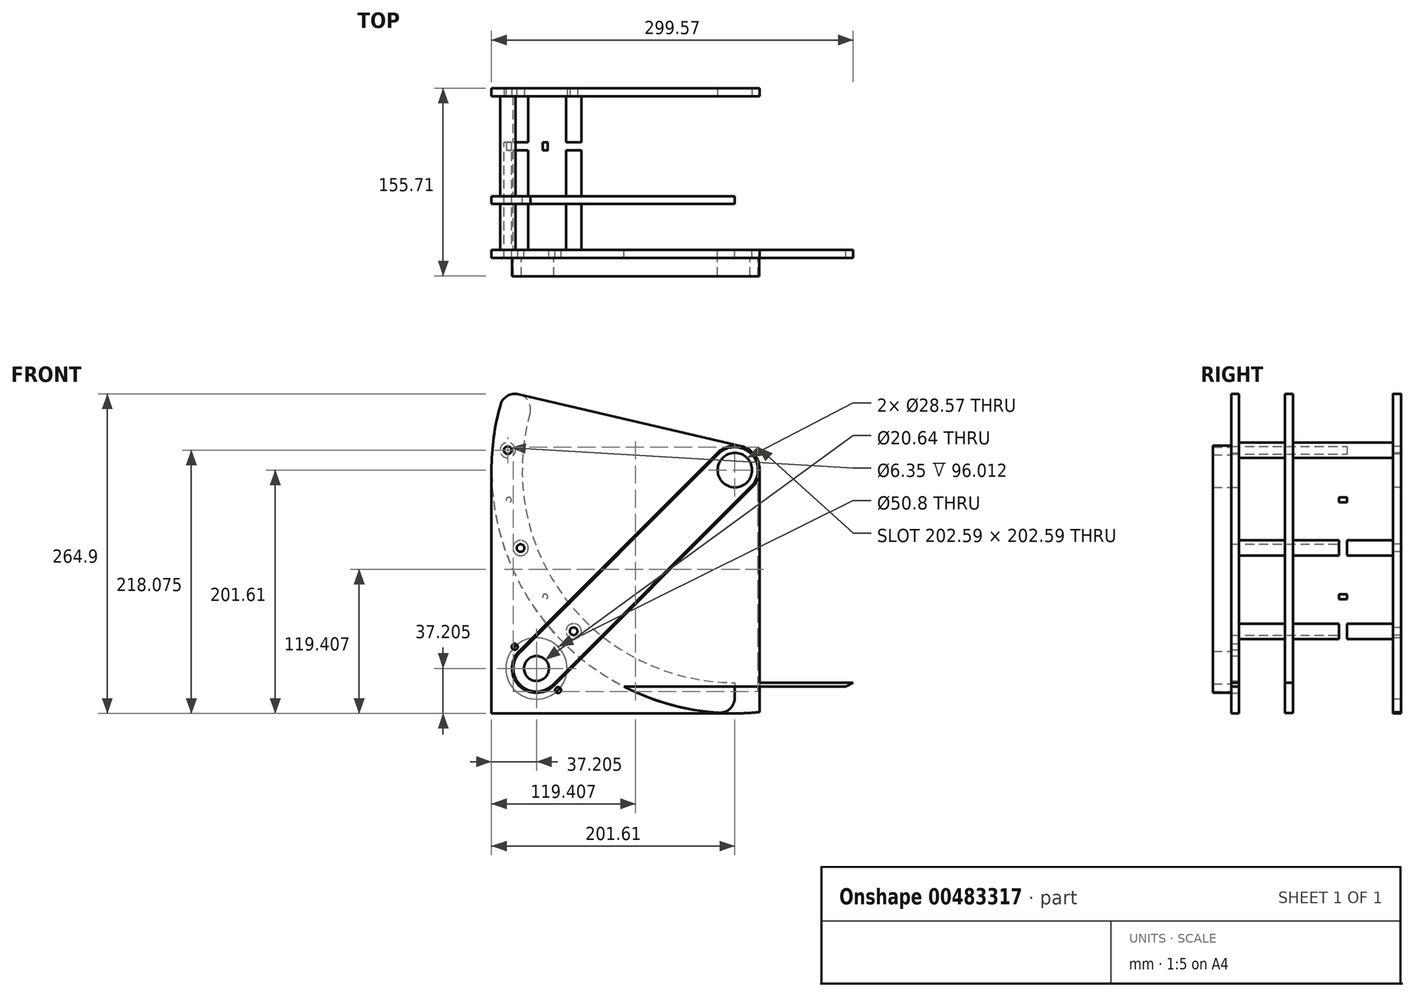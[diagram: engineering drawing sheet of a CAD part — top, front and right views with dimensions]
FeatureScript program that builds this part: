
annotation { "Feature Type Name" : "Feature", "Feature Type Description" : "" }
export const myFeature = defineFeature(function(context is Context, id is Id, definition is map)
    precondition{}
    {
        {
            var Q0;
            Q0=qCreatedBy(makeId("Front.planeOp"),FACE);
            var sketch = newSketch(context, id + "F0", { "sketchPlane" : qUnion([Q0])});
            skCircle(sketch, "E0", {"center": v(0, 0) * mm, "radius": 61.91 * mm});
            skCircle(sketch, "E1", {"center": v(0, 0) * mm, "radius": 176.21 * mm});
            skCircle(sketch, "E2.cCircle", {"center": v(0, 0) * mm, "radius": 6.35 * mm, "construction": true});
            skLineSegment(sketch, "E2.0", {"start": v(-3.67, 6.35) * mm, "end": v(3.67, 6.35) * mm});
            skLineSegment(sketch, "E2.1", {"start": v(3.67, 6.35) * mm, "end": v(7.33, 0) * mm});
            skLineSegment(sketch, "E2.2", {"start": v(7.33, 0) * mm, "end": v(3.67, -6.35) * mm});
            skLineSegment(sketch, "E2.3", {"start": v(3.67, -6.35) * mm, "end": v(-3.67, -6.35) * mm});
            skLineSegment(sketch, "E2.4", {"start": v(-3.67, -6.35) * mm, "end": v(-7.33, 0) * mm});
            skLineSegment(sketch, "E2.5", {"start": v(-7.33, 0) * mm, "end": v(-3.67, 6.35) * mm});
            skPoint(sketch, "E2.0.midPoint", {"position": v(0, 6.35) * mm});
            skCircle(sketch, "E3", {"center": v(0, 0) * mm, "radius": 201.61 * mm});
            skLineSegment(sketch, "E4", {"start": v(0, -176.21) * mm, "end": v(267.79, -176.21) * mm});
            skCircle(sketch, "E5", {"center": v(0, 0) * mm, "radius": 188.91 * mm, "construction": true});
            skCircle(sketch, "E6", {"center": v(-133.58, -133.58) * mm, "radius": 3.18 * mm});
            skLineSegment(sketch, "E7", {"start": v(0, 0) * mm, "end": v(-133.58, -133.58) * mm, "construction": true});
            skLineSegment(sketch, "E8", {"start": v(0, 0) * mm, "end": v(-190.63, 65.64) * mm});
            skCircle(sketch, "E9.1.0", {"center": v(-177.52, -64.61) * mm, "radius": 3.18 * mm});
            skCircle(sketch, "E9.2.0", {"center": v(-188.2, 16.46) * mm, "radius": 3.18 * mm});
            skCircle(sketch, "E9.3.0", {"center": v(-163.6, 94.46) * mm, "radius": 3.18 * mm});
            skLineSegment(sketch, "E9.anchor2", {"start": v(0, 0) * mm, "end": v(-163.6, 94.46) * mm, "construction": true});
            skLineSegment(sketch, "E10", {"start": v(267.83, -179.39) * mm, "end": v(-92.02, -179.39) * mm});
            skLineSegment(sketch, "E11", {"start": v(267.79, -176.21) * mm, "end": v(267.83, -179.39) * mm});
            skCircle(sketch, "E12", {"center": v(0, 0) * mm, "radius": 14.29 * mm});
            skCircle(sketch, "E13", {"center": v(0, 0) * mm, "radius": 20.64 * mm});
            skLineSegment(sketch, "E14", {"start": v(4.69, 20.1) * mm, "end": v(-190.63, 65.64) * mm});
            skLineSegment(sketch, "E15", {"start": v(20.64, 0) * mm, "end": v(20.64, -176.21) * mm});
            skLineSegment(sketch, "E16", {"start": v(20.64, -175.98) * mm, "end": v(20.64, -200.55) * mm});
            skLineSegment(sketch, "E17", {"start": v(-201.61, 0) * mm, "end": v(-201.61, -201.61) * mm});
            skLineSegment(sketch, "E18", {"start": v(-201.61, -201.61) * mm, "end": v(0, -201.61) * mm});
            skCircle(sketch, "E19", {"center": v(-164.4, -164.4) * mm, "radius": 10.32 * mm});
            skCircle(sketch, "E20", {"center": v(-146.44, -182.37) * mm, "radius": 2.49 * mm});
            skCircle(sketch, "E21", {"center": v(-182.37, -146.44) * mm, "radius": 2.49 * mm});
            skCircle(sketch, "E22", {"center": v(-164.4, -164.4) * mm, "radius": 25.4 * mm, "construction": true});
            skLineSegment(sketch, "E23", {"start": v(-146.44, -182.37) * mm, "end": v(-182.37, -146.44) * mm, "construction": true});
            skCircle(sketch, "E24", {"center": v(-164.4, -164.4) * mm, "radius": 19.1 * mm});
            skCircle(sketch, "E25", {"center": v(0, 0) * mm, "radius": 19.1 * mm});
            skLineSegment(sketch, "E26", {"start": v(-201.61, -201.61) * mm, "end": v(-133.58, -133.58) * mm, "construction": true});
            skSolve(sketch);
        }
        {
            var Q0;
            {var subQ0=sQuery(id+"F0.wireOp",EDGE,"E8");var subQ1=sQuery(id+"F0.wireOp",EDGE,"E0");var subQ2=makeQuery(id+"F0.imprint","INTERSECT",VERTEX,{"derivedFrom":[subQ1,subQ0]});Q0=makeQuery(id+"F0.imprint","IMPRINT",FACE,{"disambiguationData":[TD([[makeQuery(id+"F0.imprint","IMPRINT",EDGE,{"disambiguationData":[TD([[subQ2,1.0]])],"derivedFrom":subQ1}),1.0]])]});}
            var Q1;
            {var subQ0=sQuery(id+"F0.wireOp",EDGE,"E8");var subQ1=sQuery(id+"F0.wireOp",EDGE,"E0");var subQ2=makeQuery(id+"F0.imprint","INTERSECT",VERTEX,{"derivedFrom":[subQ1,subQ0]});Q1=makeQuery(id+"F0.imprint","IMPRINT",FACE,{"disambiguationData":[TD([[makeQuery(id+"F0.imprint","IMPRINT",EDGE,{"disambiguationData":[TD([[subQ2,1.0]])],"derivedFrom":subQ1}),-1.0]])]});}
            var Q2;
            {var subQ0=sQuery(id+"F0.wireOp",EDGE,"E8");var subQ1=sQuery(id+"F0.wireOp",EDGE,"E0");var subQ2=makeQuery(id+"F0.imprint","INTERSECT",VERTEX,{"derivedFrom":[subQ1,subQ0]});Q2=makeQuery(id+"F0.imprint","IMPRINT",FACE,{"disambiguationData":[TD([[makeQuery(id+"F0.imprint","IMPRINT",EDGE,{"disambiguationData":[TD([[subQ2,-1.0]])],"derivedFrom":subQ1}),-1.0]])]});}
            var Q3;
            {var subQ0=sQuery(id+"F0.wireOp",EDGE,"E8");var subQ1=sQuery(id+"F0.wireOp",EDGE,"E1");var subQ2=makeQuery(id+"F0.imprint","INTERSECT",VERTEX,{"derivedFrom":[subQ1,subQ0]});Q3=makeQuery(id+"F0.imprint","IMPRINT",FACE,{"disambiguationData":[TD([[makeQuery(id+"F0.imprint","IMPRINT",EDGE,{"disambiguationData":[TD([[subQ2,1.0]])],"derivedFrom":subQ1}),-1.0]])]});}
            var Q4;
            Q4=makeQuery(id+"F0.imprint","IMPRINT",FACE,{"disambiguationData":[TD([[makeQuery(id+"F0.imprint","IMPRINT",EDGE,{"derivedFrom":sQuery(id+"F0.wireOp",EDGE,"E12")}),-1.0]])]});
            var Q5;
            {var subQ0=sQuery(id+"F0.wireOp",EDGE,"E8");var subQ1=sQuery(id+"F0.wireOp",EDGE,"E0");var subQ2=makeQuery(id+"F0.imprint","INTERSECT",VERTEX,{"derivedFrom":[subQ1,subQ0]});Q5=makeQuery(id+"F0.imprint","IMPRINT",FACE,{"disambiguationData":[TD([[makeQuery(id+"F0.imprint","IMPRINT",EDGE,{"disambiguationData":[TD([[subQ2,-1.0]])],"derivedFrom":subQ1}),1.0]])]});}
            var Q6;
            {var subQ0=sQuery(id+"F0.wireOp",EDGE,"E4");var subQ1=sQuery(id+"F0.wireOp",EDGE,"E1");var subQ2=makeQuery(id+"F0.imprint","INTERSECT",VERTEX,{"derivedFrom":[subQ1,subQ0]});Q6=makeQuery(id+"F0.imprint","IMPRINT",FACE,{"disambiguationData":[TD([[makeQuery(id+"F0.imprint","IMPRINT",EDGE,{"disambiguationData":[TD([[subQ2,-1.0]])],"derivedFrom":subQ1}),-1.0]])]});}
            var Q7;
            {var subQ0=sQuery(id+"F0.wireOp",EDGE,"E10");var subQ1=sQuery(id+"F0.wireOp",EDGE,"E3");var subQ2=makeQuery(id+"F0.imprint","INTERSECT",VERTEX,{"disambiguationData":[OD(0.0)],"derivedFrom":[subQ1,subQ0]});Q7=makeQuery(id+"F0.imprint","IMPRINT",FACE,{"disambiguationData":[TD([[makeQuery(id+"F0.imprint","IMPRINT",EDGE,{"disambiguationData":[TD([[subQ2,-1.0]])],"derivedFrom":subQ1}),1.0]])]});}
            var Q8;
            Q8=makeQuery(id+"F0.imprint","IMPRINT",FACE,{"disambiguationData":[TD([[makeQuery(id+"F0.imprint","IMPRINT",EDGE,{"derivedFrom":sQuery(id+"F0.wireOp",EDGE,"E6")}),-1.0]])]});
            var Q9;
            Q9=makeQuery(id+"F0.imprint","IMPRINT",FACE,{"disambiguationData":[TD([[makeQuery(id+"F0.imprint","IMPRINT",EDGE,{"derivedFrom":sQuery(id+"F0.wireOp",EDGE,"E25")}),-1.0]])]});
            var Q10;
            {var subQ3=sQuery(id+"F0.wireOp",EDGE,"E17");Q10=makeQuery(id+"F0.imprint","IMPRINT",FACE,{"disambiguationData":[TD([[makeQuery(id+"F0.imprint","IMPRINT",EDGE,{"derivedFrom":subQ3}),1.0]])]});}
            var Q11;
            Q11=makeQuery(id+"F0.imprint","IMPRINT",FACE,{"disambiguationData":[TD([[makeQuery(id+"F0.imprint","IMPRINT",EDGE,{"derivedFrom":sQuery(id+"F0.wireOp",EDGE,"E19")}),-1.0]])]});
            extrude(context, id + "F1", {"entities" : qUnion([Q0, Q1, Q2, Q3, Q4, Q5, Q6, Q7, Q8, Q9, Q10, Q11]), "depth" : 6.6 * mm, "offsetDistance" : 25.4 * mm});
        }
        {
            var Q0;
            Q0=makeQuery(id+"F1.opExtrude","CAP_FACE",FACE,{"disambiguationData":[OSD([sQuery(id+"F0.wireOp",EDGE,"E1"),sQuery(id+"F0.wireOp",EDGE,"E3"),sQuery(id+"F0.wireOp",EDGE,"E4"),sQuery(id+"F0.wireOp",EDGE,"E6"),sQuery(id+"F0.wireOp",EDGE,"E8"),sQuery(id+"F0.wireOp",EDGE,"E9.1.0"),sQuery(id+"F0.wireOp",EDGE,"E9.2.0"),sQuery(id+"F0.wireOp",EDGE,"E9.3.0"),sQuery(id+"F0.wireOp",EDGE,"E10")])],"isStart":true});
            var sketch = newSketch(context, id + "F2", { "sketchPlane" : qUnion([Q0])});
            skCircle(sketch, "E27", {"center": v(188.2, 16.46) * mm, "radius": 6.35 * mm});
            skCircle(sketch, "E28", {"center": v(177.52, -64.61) * mm, "radius": 6.35 * mm});
            skCircle(sketch, "E29", {"center": v(133.58, -133.58) * mm, "radius": 6.35 * mm});
            skSolve(sketch);
        }
        {
            var Q0;
            Q0=makeQuery(id+"F2.imprint","IMPRINT",FACE,{"disambiguationData":[TD([[makeQuery(id+"F2.imprint","IMPRINT",EDGE,{"derivedFrom":sQuery(id+"F2.wireOp",EDGE,"E27")}),1.0]])]});
            var Q1;
            Q1=makeQuery(id+"F2.imprint","IMPRINT",FACE,{"disambiguationData":[TD([[makeQuery(id+"F2.imprint","IMPRINT",EDGE,{"derivedFrom":sQuery(id+"F2.wireOp",EDGE,"E28")}),1.0]])]});
            var Q2;
            Q2=makeQuery(id+"F2.imprint","IMPRINT",FACE,{"disambiguationData":[TD([[makeQuery(id+"F2.imprint","IMPRINT",EDGE,{"derivedFrom":sQuery(id+"F2.wireOp",EDGE,"E29")}),1.0]])]});
            extrude(context, id + "F3", {"entities" : qUnion([Q0, Q1, Q2]), "operationType" : NewBodyOperationType.ADD, "depth" : 38.1 * mm, "offsetDistance" : 25.4 * mm});
        }
        {
            var Q0;
            Q0=makeQuery(id+"F3.opExtrude","CAP_FACE",FACE,{"disambiguationData":[OSD([sQuery(id+"F0.wireOp",EDGE,"E6"),sQuery(id+"F2.wireOp",EDGE,"E29")])],"isStart":false});
            var sketch = newSketch(context, id + "F4", { "sketchPlane" : qUnion([Q0])});
            skCircle(sketch, "E30", {"center": v(0, 0) * mm, "radius": 201.61 * mm});
            skCircle(sketch, "E31", {"center": v(0, 0) * mm, "radius": 176.21 * mm});
            skLineSegment(sketch, "E32", {"start": v(133.58, 133.58) * mm, "end": v(0, 0) * mm, "construction": true});
            skCircle(sketch, "E33", {"center": v(0, 0) * mm, "radius": 188.91 * mm, "construction": true});
            skCircle(sketch, "E34.1.0", {"center": v(178.89, 60.72) * mm, "radius": 6.35 * mm});
            skCircle(sketch, "E34.2.0", {"center": v(187.3, -24.66) * mm, "radius": 6.35 * mm});
            skCircle(sketch, "E34.3.0", {"center": v(157.08, -104.95) * mm, "radius": 6.35 * mm});
            skCircle(sketch, "E34.4.0", {"center": v(94.46, -163.6) * mm, "radius": 6.35 * mm});
            skLineSegment(sketch, "E34.anchor1", {"start": v(0, 0) * mm, "end": v(133.58, 133.58) * mm, "construction": true});
            skLineSegment(sketch, "E34.anchor2", {"start": v(0, 0) * mm, "end": v(94.46, -163.6) * mm, "construction": true});
            skLineSegment(sketch, "E35.0", {"start": v(-4.69, 20.1) * mm, "end": v(190.63, 65.64) * mm});
            skCircle(sketch, "E36", {"center": v(178.89, 60.72) * mm, "radius": 3.18 * mm});
            skCircle(sketch, "E37", {"center": v(188.2, 16.46) * mm, "radius": 3.18 * mm});
            skCircle(sketch, "E38", {"center": v(187.3, -24.66) * mm, "radius": 3.18 * mm});
            skCircle(sketch, "E39", {"center": v(177.52, -64.61) * mm, "radius": 3.18 * mm});
            skCircle(sketch, "E40", {"center": v(157.08, -104.95) * mm, "radius": 3.18 * mm});
            skCircle(sketch, "E41", {"center": v(133.58, -133.58) * mm, "radius": 3.18 * mm});
            skLineSegment(sketch, "E42", {"start": v(0, 0) * mm, "end": v(0, -201.61) * mm});
            skSolve(sketch);
        }
        {
            var Q0;
            Q0=makeQuery(id+"F4.imprint","IMPRINT",FACE,{"disambiguationData":[TD([[makeQuery(id+"F4.imprint","IMPRINT",EDGE,{"derivedFrom":sQuery(id+"F4.wireOp",EDGE,"E34.2.0")}),-1.0]])]});
            var Q1;
            Q1=makeQuery(id+"F4.imprint","IMPRINT",FACE,{"disambiguationData":[TD([[makeQuery(id+"F4.imprint","IMPRINT",EDGE,{"derivedFrom":sQuery(id+"F4.wireOp",EDGE,"E41")}),1.0]])]});
            var Q2;
            {var subQ0=sQuery(id+"F4.wireOp",EDGE,"E35.0");var subQ1=sQuery(id+"F4.wireOp",EDGE,"E34.1.0");var subQ2=makeQuery(id+"F4.imprint","INTERSECT",VERTEX,{"disambiguationData":[OD(0.0)],"derivedFrom":[subQ1,subQ0]});Q2=makeQuery(id+"F4.imprint","IMPRINT",FACE,{"disambiguationData":[TD([[makeQuery(id+"F4.imprint","IMPRINT",EDGE,{"disambiguationData":[TD([[subQ2,-1.0]])],"derivedFrom":subQ1}),1.0]])]});}
            var Q3;
            {var subQ0=sQuery(id+"F4.wireOp",EDGE,"E36");var subQ1=sQuery(id+"F4.wireOp",EDGE,"E35.0");var subQ2=makeQuery(id+"F4.imprint","INTERSECT",VERTEX,{"disambiguationData":[OD(0.0)],"derivedFrom":[subQ1,subQ0]});Q3=makeQuery(id+"F4.imprint","IMPRINT",FACE,{"disambiguationData":[TD([[makeQuery(id+"F4.imprint","IMPRINT",EDGE,{"disambiguationData":[TD([[subQ2,-1.0]])],"derivedFrom":subQ1}),-1.0]])]});}
            var Q4;
            Q4=makeQuery(id+"F4.imprint","IMPRINT",FACE,{"disambiguationData":[TD([[makeQuery(id+"F4.imprint","IMPRINT",EDGE,{"derivedFrom":sQuery(id+"F4.wireOp",EDGE,"E34.4.0")}),1.0]])]});
            var Q5;
            Q5=makeQuery(id+"F4.imprint","IMPRINT",FACE,{"disambiguationData":[TD([[makeQuery(id+"F4.imprint","IMPRINT",EDGE,{"derivedFrom":sQuery(id+"F4.wireOp",EDGE,"E34.3.0")}),1.0]])]});
            var Q6;
            Q6=makeQuery(id+"F4.imprint","IMPRINT",FACE,{"disambiguationData":[TD([[makeQuery(id+"F4.imprint","IMPRINT",EDGE,{"derivedFrom":sQuery(id+"F4.wireOp",EDGE,"E40")}),1.0]])]});
            var Q7;
            Q7=makeQuery(id+"F4.imprint","IMPRINT",FACE,{"disambiguationData":[TD([[makeQuery(id+"F4.imprint","IMPRINT",EDGE,{"derivedFrom":sQuery(id+"F4.wireOp",EDGE,"E34.2.0")}),1.0]])]});
            var Q8;
            Q8=makeQuery(id+"F4.imprint","IMPRINT",FACE,{"disambiguationData":[TD([[makeQuery(id+"F4.imprint","IMPRINT",EDGE,{"derivedFrom":sQuery(id+"F4.wireOp",EDGE,"E38")}),1.0]])]});
            extrude(context, id + "F5", {"entities" : qUnion([Q0, Q1, Q2, Q3, Q4, Q5, Q6, Q7, Q8]), "operationType" : NewBodyOperationType.ADD, "depth" : 6.6 * mm, "offsetDistance" : 25.4 * mm});
        }
        {
            var Q0;
            Q0=makeQuery(id+"F5.opExtrude","CAP_FACE",FACE,{"disambiguationData":[OSD([sQuery(id+"F4.wireOp",EDGE,"E30"),sQuery(id+"F4.wireOp",EDGE,"E31"),sQuery(id+"F4.wireOp",EDGE,"E35.0"),sQuery(id+"F4.wireOp",EDGE,"8neH0s6F-ErBh-p7Tc-FeBG-JO8hClFv3z9E"),sQuery(id+"F4.wireOp",EDGE,"E36"),sQuery(id+"F4.wireOp",EDGE,"E37"),sQuery(id+"F4.wireOp",EDGE,"E38"),sQuery(id+"F4.wireOp",EDGE,"E39"),sQuery(id+"F4.wireOp",EDGE,"E40"),sQuery(id+"F4.wireOp",EDGE,"E41"),sQuery(id+"F4.wireOp",EDGE,"E42")])],"isStart":false});
            var sketch = newSketch(context, id + "F6", { "sketchPlane" : qUnion([Q0])});
            skCircle(sketch, "E43", {"center": v(178.89, 60.72) * mm, "radius": 6.35 * mm});
            skCircle(sketch, "E44", {"center": v(187.3, -24.66) * mm, "radius": 6.35 * mm});
            skCircle(sketch, "E45", {"center": v(157.08, -104.95) * mm, "radius": 6.35 * mm});
            skCircle(sketch, "E46", {"center": v(188.2, 16.46) * mm, "radius": 6.35 * mm});
            skCircle(sketch, "E47", {"center": v(177.52, -64.61) * mm, "radius": 6.35 * mm});
            skCircle(sketch, "E48", {"center": v(133.58, -133.58) * mm, "radius": 6.35 * mm});
            skSolve(sketch);
        }
        {
            var Q0;
            Q0=makeQuery(id+"F6.imprint","IMPRINT",FACE,{"disambiguationData":[TD([[makeQuery(id+"F6.imprint","IMPRINT",EDGE,{"derivedFrom":sQuery(id+"F6.wireOp",EDGE,"E46")}),1.0]])]});
            var Q1;
            Q1=makeQuery(id+"F6.imprint","IMPRINT",FACE,{"disambiguationData":[TD([[makeQuery(id+"F6.imprint","IMPRINT",EDGE,{"derivedFrom":sQuery(id+"F6.wireOp",EDGE,"E47")}),1.0]])]});
            var Q2;
            Q2=makeQuery(id+"F6.imprint","IMPRINT",FACE,{"disambiguationData":[TD([[makeQuery(id+"F6.imprint","IMPRINT",EDGE,{"derivedFrom":sQuery(id+"F6.wireOp",EDGE,"E48")}),1.0]])]});
            extrude(context, id + "F7", {"entities" : qUnion([Q0, Q1, Q2]), "operationType" : NewBodyOperationType.ADD, "depth" : 38.1 * mm, "offsetDistance" : 25.4 * mm});
        }
        {
            var Q0;
            Q0=makeQuery(id+"F7.opExtrude","CAP_FACE",FACE,{"disambiguationData":[OSD([sQuery(id+"F4.wireOp",EDGE,"E37"),sQuery(id+"F6.wireOp",EDGE,"E46")])],"isStart":false});
            var sketch = newSketch(context, id + "F8", { "sketchPlane" : qUnion([Q0])});
            skCircle(sketch, "E49.0", {"center": v(163.6, 94.46) * mm, "radius": 2.15 * mm});
            skArc(sketch, "E50.1", {"start": v(0, -176.21) * mm, "mid": v(144.21, -101.26) * mm, "end": v(165.74, 59.84) * mm});
            skPoint(sketch, "E51.0", {"position": v(178.19, 62.74) * mm});
            skLineSegment(sketch, "E52.0", {"start": v(165.74, 59.84) * mm, "end": v(190.63, 65.64) * mm});
            skLineSegment(sketch, "E53.0.0", {"start": v(190.63, 65.64) * mm, "end": v(165.74, 59.84) * mm});
            skArc(sketch, "E53.0.1", {"start": v(165.74, 59.84) * mm, "mid": v(144.21, -101.26) * mm, "end": v(0, -176.21) * mm});
            skLineSegment(sketch, "E53.0.2", {"start": v(0, -176.21) * mm, "end": v(0, -201.61) * mm});
            skArc(sketch, "E53.0.3", {"start": v(0, -201.61) * mm, "mid": v(164.14, -117.08) * mm, "end": v(190.63, 65.64) * mm});
            skCircle(sketch, "E54.0", {"center": v(188.2, 16.46) * mm, "radius": 2.15 * mm});
            skCircle(sketch, "E55.0", {"center": v(177.52, -64.61) * mm, "radius": 2.15 * mm});
            skCircle(sketch, "E56.0", {"center": v(133.58, -133.58) * mm, "radius": 2.15 * mm});
            skCircle(sketch, "E57.0", {"center": v(157.08, -104.95) * mm, "radius": 2.15 * mm});
            skCircle(sketch, "E58.0", {"center": v(187.3, -24.66) * mm, "radius": 2.15 * mm});
            skCircle(sketch, "E59.0", {"center": v(178.89, 60.72) * mm, "radius": 2.15 * mm});
            skSolve(sketch);
        }
        {
            var Q0;
            {var subQ5=sQuery(id+"F8.wireOp",EDGE,"E53.0.1");Q0=makeQuery(id+"F8.imprint","IMPRINT",FACE,{"disambiguationData":[TD([[makeQuery(id+"F8.imprint","IMPRINT",EDGE,{"derivedFrom":subQ5}),1.0]])]});}
            var Q1;
            {var subQ0=sQuery(id+"F8.wireOp",EDGE,"E59.0");var subQ1=sQuery(id+"F8.wireOp",EDGE,"E53.0.0");var subQ2=makeQuery(id+"F8.imprint","INTERSECT",VERTEX,{"disambiguationData":[OD(0.0)],"derivedFrom":[subQ1,subQ0]});Q1=makeQuery(id+"F8.imprint","IMPRINT",FACE,{"disambiguationData":[TD([[makeQuery(id+"F8.imprint","IMPRINT",EDGE,{"disambiguationData":[TD([[subQ2,-1.0]])],"derivedFrom":subQ1}),1.0]])]});}
            var Q2;
            Q2=makeQuery(id+"F8.imprint","IMPRINT",FACE,{"disambiguationData":[TD([[makeQuery(id+"F8.imprint","IMPRINT",EDGE,{"derivedFrom":makeQuery(id+"F7.opExtrude","CAP_EDGE",EDGE,{"disambiguationData":[OSD([sQuery(id+"F6.wireOp",EDGE,"E46")])],"isStart":false})}),1.0]])]});
            var Q3;
            Q3=makeQuery(id+"F8.imprint","IMPRINT",FACE,{"disambiguationData":[TD([[makeQuery(id+"F8.imprint","IMPRINT",EDGE,{"derivedFrom":sQuery(id+"F8.wireOp",EDGE,"E58.0")}),1.0]])]});
            var Q4;
            Q4=makeQuery(id+"F8.imprint","IMPRINT",FACE,{"disambiguationData":[TD([[makeQuery(id+"F8.imprint","IMPRINT",EDGE,{"derivedFrom":sQuery(id+"F8.wireOp",EDGE,"E57.0")}),1.0]])]});
            extrude(context, id + "F9", {"entities" : qUnion([Q0, Q1, Q2, Q3, Q4]), "operationType" : NewBodyOperationType.ADD, "depth" : 6.6 * mm, "offsetDistance" : 25.4 * mm});
        }
        {
            var Q0;
            Q0=makeQuery(id+"F9.opExtrude","CAP_FACE",FACE,{"disambiguationData":[OSD([sQuery(id+"F8.wireOp",EDGE,"E49.0"),sQuery(id+"F8.wireOp",EDGE,"E53.0.0"),sQuery(id+"F8.wireOp",EDGE,"E53.0.1"),sQuery(id+"F8.wireOp",EDGE,"E53.0.2"),sQuery(id+"F8.wireOp",EDGE,"E53.0.3"),sQuery(id+"F8.wireOp",EDGE,"E54.0"),sQuery(id+"F8.wireOp",EDGE,"E55.0"),sQuery(id+"F8.wireOp",EDGE,"E56.0"),sQuery(id+"F8.wireOp",EDGE,"E57.0"),sQuery(id+"F8.wireOp",EDGE,"E58.0"),sQuery(id+"F8.wireOp",EDGE,"E59.0")])],"isStart":false});
            var sketch = newSketch(context, id + "F10", { "sketchPlane" : qUnion([Q0])});
            skCircle(sketch, "E60.0", {"center": v(163.6, 94.46) * mm, "radius": 6.35 * mm});
            skCircle(sketch, "E61.0", {"center": v(188.2, 16.46) * mm, "radius": 6.35 * mm});
            skCircle(sketch, "E62.1", {"center": v(177.52, -64.61) * mm, "radius": 6.35 * mm});
            skCircle(sketch, "E63.0", {"center": v(133.58, -133.58) * mm, "radius": 6.35 * mm});
            skCircle(sketch, "E64", {"center": v(178.89, 60.72) * mm, "radius": 6.35 * mm});
            skCircle(sketch, "E65", {"center": v(187.3, -24.66) * mm, "radius": 6.35 * mm});
            skCircle(sketch, "E66", {"center": v(157.08, -104.95) * mm, "radius": 6.35 * mm});
            skSolve(sketch);
        }
        {
            var Q0;
            Q0=makeQuery(id+"F10.imprint","IMPRINT",FACE,{"disambiguationData":[TD([[makeQuery(id+"F10.imprint","IMPRINT",EDGE,{"derivedFrom":sQuery(id+"F10.wireOp",EDGE,"E61.0")}),1.0]])]});
            var Q1;
            Q1=makeQuery(id+"F10.imprint","IMPRINT",FACE,{"disambiguationData":[TD([[makeQuery(id+"F10.imprint","IMPRINT",EDGE,{"derivedFrom":sQuery(id+"F10.wireOp",EDGE,"E62.1")}),1.0]])]});
            var Q2;
            Q2=makeQuery(id+"F10.imprint","IMPRINT",FACE,{"disambiguationData":[TD([[makeQuery(id+"F10.imprint","IMPRINT",EDGE,{"derivedFrom":sQuery(id+"F10.wireOp",EDGE,"E63.0")}),1.0]])]});
            extrude(context, id + "F11", {"entities" : qUnion([Q0, Q1, Q2]), "operationType" : NewBodyOperationType.ADD, "depth" : 38.1 * mm, "offsetDistance" : 25.4 * mm});
        }
        {
            var Q0;
            Q0=makeQuery(id+"F11.opExtrude","CAP_FACE",FACE,{"disambiguationData":[OSD([sQuery(id+"F4.wireOp",EDGE,"E37"),sQuery(id+"F10.wireOp",EDGE,"E61.0")])],"isStart":false});
            var sketch = newSketch(context, id + "F12", { "sketchPlane" : qUnion([Q0])});
            skLineSegment(sketch, "E67.0", {"start": v(-4.69, 20.1) * mm, "end": v(190.63, 65.64) * mm});
            skArc(sketch, "E68.0", {"start": v(-20.64, 0) * mm, "mid": v(-16.17, 12.83) * mm, "end": v(-4.69, 20.1) * mm});
            skLineSegment(sketch, "E69.0", {"start": v(-20.64, 0) * mm, "end": v(-20.64, -176.21) * mm});
            skCircle(sketch, "E70.0", {"center": v(0, 0) * mm, "radius": 14.29 * mm});
            skCircle(sketch, "E71.0", {"center": v(163.6, 94.46) * mm, "radius": 3.18 * mm});
            skCircle(sketch, "E72.0", {"center": v(188.2, 16.46) * mm, "radius": 3.18 * mm});
            skCircle(sketch, "E73.0", {"center": v(177.52, -64.61) * mm, "radius": 3.18 * mm});
            skCircle(sketch, "E74.0", {"center": v(133.58, -133.58) * mm, "radius": 3.18 * mm});
            skLineSegment(sketch, "E75.0", {"start": v(-20.64, -176.21) * mm, "end": v(-20.64, -176.21) * mm});
            skLineSegment(sketch, "E76", {"start": v(-20.64, -176.21) * mm, "end": v(-20.64, -200.55) * mm});
            skLineSegment(sketch, "E77.0", {"start": v(201.61, 0) * mm, "end": v(201.61, -201.61) * mm});
            skLineSegment(sketch, "E78.0", {"start": v(201.61, -201.61) * mm, "end": v(0, -201.61) * mm});
            skArc(sketch, "E79.0", {"start": v(0, -201.61) * mm, "mid": v(-10.33, -201.35) * mm, "end": v(-20.64, -200.55) * mm});
            skArc(sketch, "E80.0", {"start": v(190.63, 65.64) * mm, "mid": v(198.85, 33.28) * mm, "end": v(201.61, 0) * mm});
            skCircle(sketch, "E81.0", {"center": v(164.4, -164.4) * mm, "radius": 10.32 * mm});
            skCircle(sketch, "E82", {"center": v(164.4, -164.4) * mm, "radius": 25.4 * mm});
            skSolve(sketch);
        }
        {
            var Q0;
            Q0=makeQuery(id+"F12.imprint","IMPRINT",FACE,{"disambiguationData":[TD([[makeQuery(id+"F12.imprint","IMPRINT",EDGE,{"derivedFrom":sQuery(id+"F12.wireOp",EDGE,"E67.0")}),-1.0]])]});
            var Q1;
            Q1=makeQuery(id+"F12.imprint","IMPRINT",FACE,{"disambiguationData":[TD([[makeQuery(id+"F12.imprint","IMPRINT",EDGE,{"derivedFrom":sQuery(id+"F12.wireOp",EDGE,"E72.0")}),-1.0]])]});
            extrude(context, id + "F13", {"entities" : qUnion([Q0, Q1]), "operationType" : NewBodyOperationType.ADD, "depth" : 6.6 * mm, "offsetDistance" : 25.4 * mm});
        }
        {
            var Q0;
            Q0=makeQuery(id+"F1.opExtrude","SWEPT_EDGE",EDGE,{"disambiguationData":[OSD([sQuery(id+"F0.wireOp",EDGE,"E3"),sQuery(id+"F0.wireOp",EDGE,"E8"),sQuery(id+"F0.wireOp",EDGE,"E14")])]});
            var Q1;
            Q1=makeQuery(id+"F5.opExtrude","SWEPT_EDGE",EDGE,{"disambiguationData":[OSD([sQuery(id+"F4.wireOp",EDGE,"E30"),sQuery(id+"F4.wireOp",EDGE,"E35.0")])]});
            var Q2;
            Q2=makeQuery(id+"F9.opExtrude","SWEPT_EDGE",EDGE,{"disambiguationData":[OSD([sQuery(id+"F8.wireOp",EDGE,"E53.0.0"),sQuery(id+"F8.wireOp",EDGE,"E53.0.1")])]});
            var Q3;
            Q3=makeQuery(id+"F9.opExtrude","SWEPT_EDGE",EDGE,{"disambiguationData":[OSD([sQuery(id+"F8.wireOp",EDGE,"E53.0.0"),sQuery(id+"F8.wireOp",EDGE,"E53.0.3")])]});
            var Q4;
            Q4=makeQuery(id+"F5.opExtrude","SWEPT_EDGE",EDGE,{"disambiguationData":[OSD([sQuery(id+"F4.wireOp",EDGE,"E31"),sQuery(id+"F4.wireOp",EDGE,"E35.0")])]});
            var Q5;
            Q5=makeQuery(id+"F13.opExtrude","SWEPT_EDGE",EDGE,{"disambiguationData":[OSD([sQuery(id+"F12.wireOp",EDGE,"E67.0"),sQuery(id+"F12.wireOp",EDGE,"E80.0")])]});
            var Q6;
            Q6=makeQuery(id+"F5.opExtrude","SWEPT_EDGE",EDGE,{"disambiguationData":[OSD([sQuery(id+"F4.wireOp",EDGE,"E30"),sQuery(id+"F4.wireOp",EDGE,"E42")])]});
            var Q7;
            Q7=makeQuery(id+"F9.opExtrude","SWEPT_EDGE",EDGE,{"disambiguationData":[OSD([sQuery(id+"F8.wireOp",EDGE,"E53.0.2"),sQuery(id+"F8.wireOp",EDGE,"E53.0.3")])]});
            fillet(context, id + "F14", {"entities" : qUnion([Q0, Q1, Q2, Q3, Q4, Q5, Q6, Q7]), "radius" : 12.7 * mm, "tangentPropagation" : true, "allowEdgeOverflow" : false});
        }
        {
            var Q0;
            Q0=makeQuery(id+"F1.opExtrude","CAP_FACE",FACE,{"disambiguationData":[OSD([sQuery(id+"F0.wireOp",EDGE,"E3"),sQuery(id+"F0.wireOp",EDGE,"E4"),sQuery(id+"F0.wireOp",EDGE,"E6"),sQuery(id+"F0.wireOp",EDGE,"E9.1.0"),sQuery(id+"F0.wireOp",EDGE,"E9.2.0"),sQuery(id+"F0.wireOp",EDGE,"E9.3.0"),sQuery(id+"F0.wireOp",EDGE,"E12"),sQuery(id+"F0.wireOp",EDGE,"E13"),sQuery(id+"F0.wireOp",EDGE,"E14"),sQuery(id+"F0.wireOp",EDGE,"E15"),sQuery(id+"F0.wireOp",EDGE,"E16"),sQuery(id+"F0.wireOp",EDGE,"E17"),sQuery(id+"F0.wireOp",EDGE,"E18"),sQuery(id+"F0.wireOp",EDGE,"E19"),sQuery(id+"F0.wireOp",EDGE,"E20"),sQuery(id+"F0.wireOp",EDGE,"E21")])],"isStart":false});
            var sketch = newSketch(context, id + "F15", { "sketchPlane" : qUnion([Q0])});
            skCircle(sketch, "E83.0", {"center": v(0, 0) * mm, "radius": 19.1 * mm});
            skCircle(sketch, "E84.0", {"center": v(-164.4, -164.4) * mm, "radius": 19.1 * mm});
            skCircle(sketch, "E85", {"center": v(-164.4, -164.4) * mm, "radius": 20.24 * mm});
            skCircle(sketch, "E86", {"center": v(0, 0) * mm, "radius": 20.24 * mm});
            skLineSegment(sketch, "E87", {"start": v(-178.72, -150.1) * mm, "end": v(-14.31, 14.31) * mm});
            skLineSegment(sketch, "E88", {"start": v(-177.05, -150.1) * mm, "end": v(-14.31, 12.65) * mm});
            skLineSegment(sketch, "E89.MirrorCS", {"start": v(-150.1, -178.72) * mm, "end": v(14.31, -14.31) * mm});
            skLineSegment(sketch, "E90.MirrorCS", {"start": v(-150.1, -177.05) * mm, "end": v(12.65, -14.31) * mm});
            skSolve(sketch);
        }
        {
            var Q0;
            Q0 = qSketchRegion(id + "F15", true);
            extrude(context, id + "F16", {"entities" : qUnion([Q0]), "depth" : 15 * mm});
        }
    });
